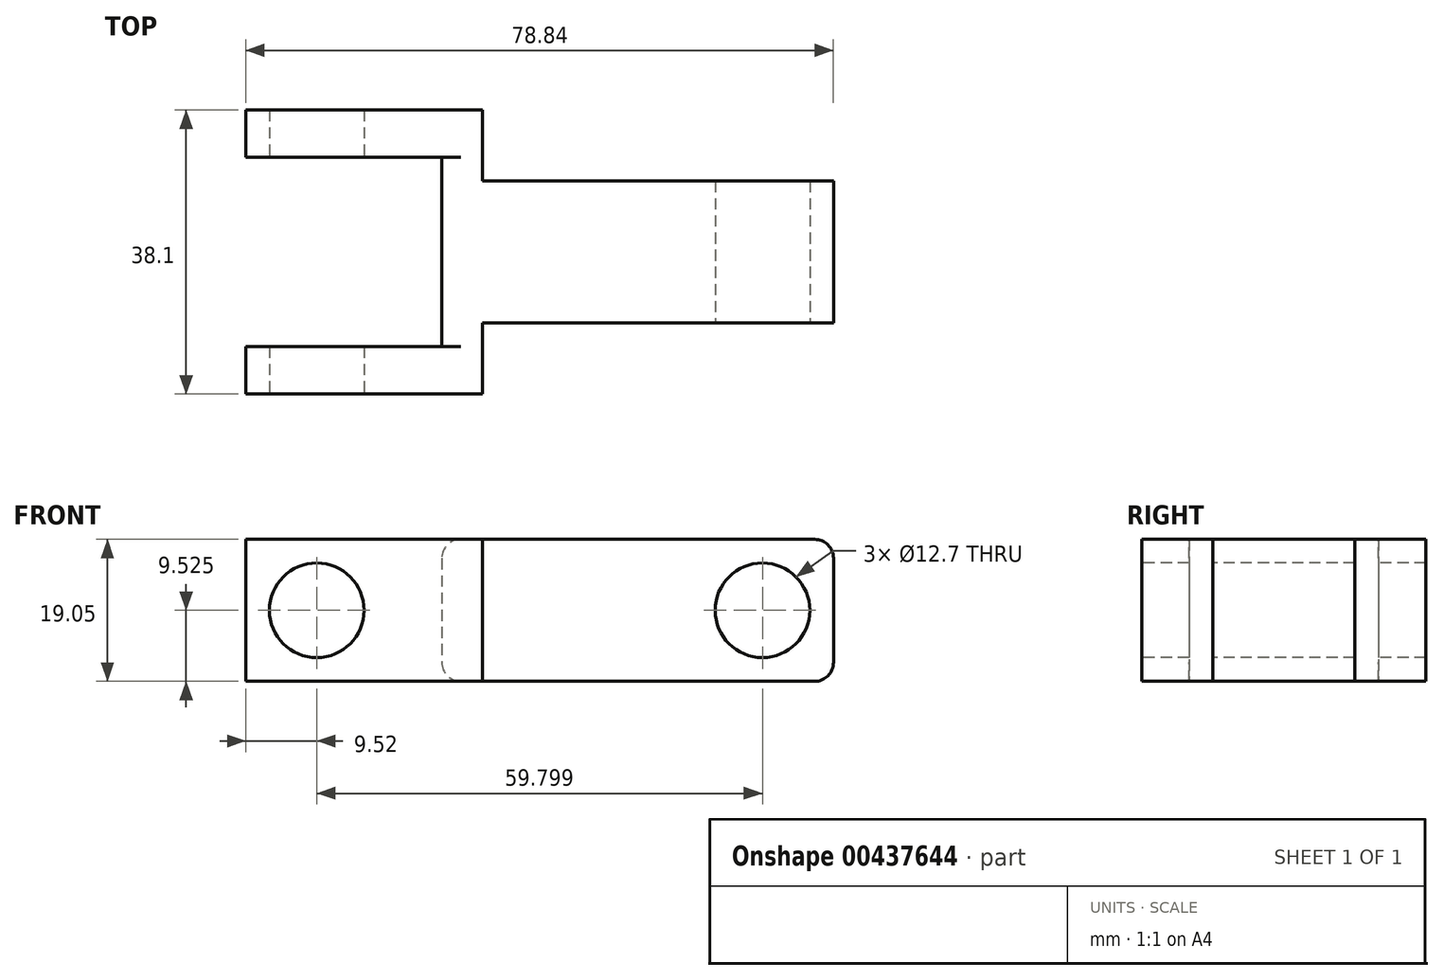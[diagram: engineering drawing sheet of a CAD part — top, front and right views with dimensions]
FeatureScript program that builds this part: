
annotation { "Feature Type Name" : "Feature", "Feature Type Description" : "" }
export const myFeature = defineFeature(function(context is Context, id is Id, definition is map)
    precondition{}
    {
        {
            var Q0;
            Q0=qCreatedBy(makeId("Top.planeOp"),FACE);
            var sketch = newSketch(context, id + "F0", { "sketchPlane" : qUnion([Q0])});
            skLineSegment(sketch, "E0.bottom", {"start": v(-1.7, -4.04) * mm, "end": v(45.4, -4.04) * mm});
            skLineSegment(sketch, "E0.top", {"start": v(-1.7, -23.09) * mm, "end": v(45.4, -23.09) * mm});
            skLineSegment(sketch, "E0.left", {"start": v(-33.44, 5.49) * mm, "end": v(-33.44, -0.86) * mm});
            skLineSegment(sketch, "E0.right", {"start": v(45.4, -4.04) * mm, "end": v(45.4, -23.09) * mm});
            skLineSegment(sketch, "E1", {"start": v(-33.44, 5.49) * mm, "end": v(-1.7, 5.49) * mm});
            skLineSegment(sketch, "E2", {"start": v(-33.44, -32.61) * mm, "end": v(-1.7, -32.61) * mm});
            skLineSegment(sketch, "E3", {"start": v(-1.7, -32.61) * mm, "end": v(-1.7, -23.09) * mm});
            skPoint(sketch, "E4.orphan", {"position": v(0, 5.49) * mm});
            skLineSegment(sketch, "E5.trimOffspring", {"start": v(-1.7, -4.04) * mm, "end": v(-1.7, 5.49) * mm});
            skLineSegment(sketch, "E6.bottom", {"start": v(-33.44, -0.86) * mm, "end": v(-7.15, -0.86) * mm});
            skLineSegment(sketch, "E6.top", {"start": v(-33.44, -26.26) * mm, "end": v(-7.15, -26.26) * mm});
            skLineSegment(sketch, "E6.right", {"start": v(-7.15, -0.86) * mm, "end": v(-7.15, -26.26) * mm});
            skLineSegment(sketch, "E7.trimOffspring", {"start": v(-33.44, -26.26) * mm, "end": v(-33.44, -32.61) * mm});
            skSolve(sketch);
        }
        {
            var Q0;
            Q0=makeQuery(id+"F0.imprint","IMPRINT",FACE,{"disambiguationData":[TD([[makeQuery(id+"F0.imprint","IMPRINT",EDGE,{"derivedFrom":sQuery(id+"F0.wireOp",EDGE,"E0.bottom")}),-1.0]])]});
            extrude(context, id + "F1", {"entities" : qUnion([Q0]), "depth" : 19.05 * mm});
        }
        {
            var Q0;
            Q0=makeQuery(id+"F1.opExtrude","SWEPT_FACE",FACE,{"disambiguationData":[OSD([sQuery(id+"F0.wireOp",EDGE,"E2")])]});
            var sketch = newSketch(context, id + "F2", { "sketchPlane" : qUnion([Q0])});
            skPoint(sketch, "E8", {"position": v(-23.92, 9.53) * mm});
            skSolve(sketch);
        }
        {
            var Q0;
            Q0=sQuery(id+"F2.wireOp",VERTEX,"E8");
            var Q1;
            Q1=makeQuery(id+"F1.opExtrude","SWEPT_BODY",BODY,{"disambiguationData":[OSD([sQuery(id+"F0.wireOp",EDGE,"E0.bottom"),sQuery(id+"F0.wireOp",EDGE,"E0.top"),sQuery(id+"F0.wireOp",EDGE,"E0.left"),sQuery(id+"F0.wireOp",EDGE,"E0.right"),sQuery(id+"F0.wireOp",EDGE,"E1"),sQuery(id+"F0.wireOp",EDGE,"E2"),sQuery(id+"F0.wireOp",EDGE,"E3"),sQuery(id+"F0.wireOp",EDGE,"E5.trimOffspring"),sQuery(id+"F0.wireOp",EDGE,"E6.bottom"),sQuery(id+"F0.wireOp",EDGE,"E6.top"),sQuery(id+"F0.wireOp",EDGE,"E6.right"),sQuery(id+"F0.wireOp",EDGE,"E7.trimOffspring")])]});
            hole(context, id + "F3", {"style" : HoleStyle.SIMPLE, "endStyle" : HoleEndStyle.THROUGH, "holeDiameter" : 12.7 * mm, "isTappedThrough" : true, "tappedDepth" : 12.7 * mm, "tapClearance" : 3, "locations" : qUnion([Q0]), "scope" : qUnion([Q1])});
        }
        {
            var Q0;
            Q0=makeQuery(id+"F1.opExtrude","SWEPT_FACE",FACE,{"disambiguationData":[OSD([sQuery(id+"F0.wireOp",EDGE,"E0.top")])]});
            var sketch = newSketch(context, id + "F4", { "sketchPlane" : qUnion([Q0])});
            skLineSegment(sketch, "E9.bottom", {"start": v(45.4, 19.05) * mm, "end": v(35.88, 19.05) * mm});
            skLineSegment(sketch, "E9.top", {"start": v(45.4, 9.52) * mm, "end": v(35.88, 9.52) * mm});
            skLineSegment(sketch, "E9.left", {"start": v(45.4, 19.05) * mm, "end": v(45.4, 9.52) * mm});
            skLineSegment(sketch, "E9.right", {"start": v(35.88, 19.05) * mm, "end": v(35.88, 9.52) * mm});
            skSolve(sketch);
        }
        {
            var Q0;
            Q0=sQuery(id+"F4.wireOp",VERTEX,"E9.right.end");
            var Q1;
            Q1=makeQuery(id+"F1.opExtrude","SWEPT_BODY",BODY,{"disambiguationData":[OSD([sQuery(id+"F0.wireOp",EDGE,"E0.bottom"),sQuery(id+"F0.wireOp",EDGE,"E0.top"),sQuery(id+"F0.wireOp",EDGE,"E0.left"),sQuery(id+"F0.wireOp",EDGE,"E0.right"),sQuery(id+"F0.wireOp",EDGE,"E1"),sQuery(id+"F0.wireOp",EDGE,"E2"),sQuery(id+"F0.wireOp",EDGE,"E3"),sQuery(id+"F0.wireOp",EDGE,"E5.trimOffspring"),sQuery(id+"F0.wireOp",EDGE,"E6.bottom"),sQuery(id+"F0.wireOp",EDGE,"E6.top"),sQuery(id+"F0.wireOp",EDGE,"E6.right"),sQuery(id+"F0.wireOp",EDGE,"E7.trimOffspring")])]});
            hole(context, id + "F5", {"style" : HoleStyle.SIMPLE, "endStyle" : HoleEndStyle.THROUGH, "holeDiameter" : 12.7 * mm, "isTappedThrough" : true, "tappedDepth" : 12.7 * mm, "tapClearance" : 3, "startFromSketch" : true, "locations" : qUnion([Q0]), "scope" : qUnion([Q1])});
        }
        {
            var Q0;
            Q0=makeQuery(id+"F1.opExtrude","CAP_EDGE",EDGE,{"disambiguationData":[OSD([sQuery(id+"F0.wireOp",EDGE,"E0.right")])],"isStart":false});
            var Q1;
            Q1=makeQuery(id+"F1.opExtrude","CAP_EDGE",EDGE,{"disambiguationData":[OSD([sQuery(id+"F0.wireOp",EDGE,"E0.right")])],"isStart":true});
            var Q2;
            Q2=makeQuery(id+"F1.opExtrude","CAP_EDGE",EDGE,{"disambiguationData":[OSD([sQuery(id+"F0.wireOp",EDGE,"E6.right")])],"isStart":false});
            var Q3;
            Q3=makeQuery(id+"F1.opExtrude","CAP_EDGE",EDGE,{"disambiguationData":[OSD([sQuery(id+"F0.wireOp",EDGE,"E6.right")])],"isStart":true});
            fillet(context, id + "F6", {"entities" : qUnion([Q0, Q1, Q2, Q3]), "radius" : 2.54 * mm, "tangentPropagation" : true, "allowEdgeOverflow" : false});
        }
    });
